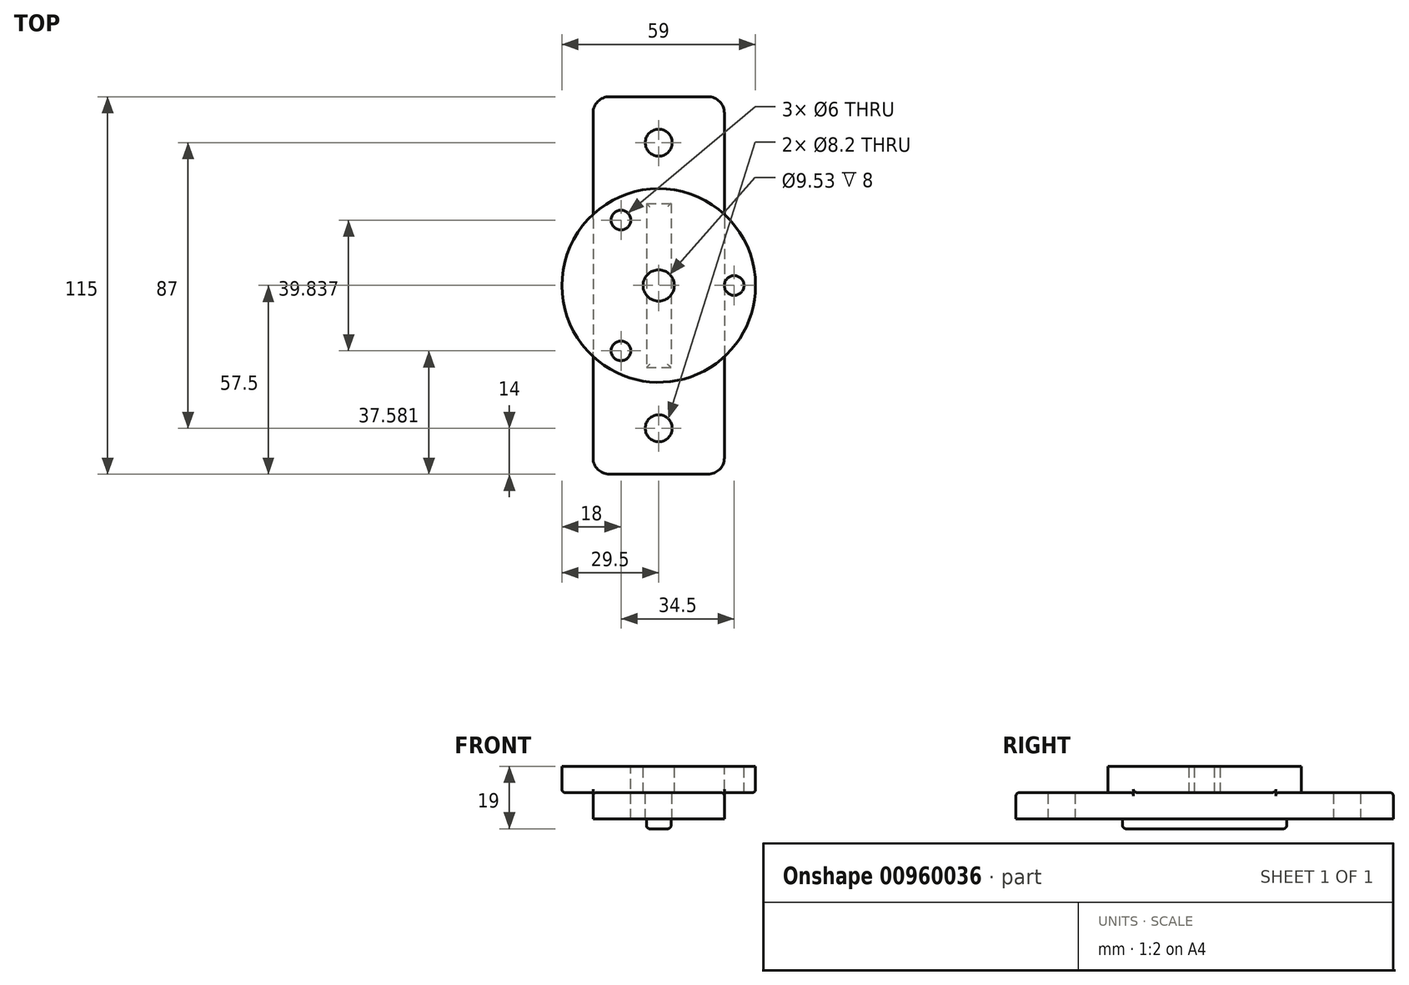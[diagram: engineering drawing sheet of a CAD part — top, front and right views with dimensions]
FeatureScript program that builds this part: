
annotation { "Feature Type Name" : "Feature", "Feature Type Description" : "" }
export const myFeature = defineFeature(function(context is Context, id is Id, definition is map)
    precondition{}
    {
        {
            var Q0;
            Q0=qCreatedBy(makeId("Top.planeOp"),FACE);
            var sketch = newSketch(context, id + "F0", { "sketchPlane" : qUnion([Q0])});
            skLineSegment(sketch, "E0.bottom", {"start": v(20, 57.5) * mm, "end": v(-20, 57.5) * mm});
            skLineSegment(sketch, "E0.top", {"start": v(20, -57.5) * mm, "end": v(-20, -57.5) * mm});
            skLineSegment(sketch, "E0.left", {"start": v(20, 57.5) * mm, "end": v(20, -57.5) * mm});
            skLineSegment(sketch, "E0.right", {"start": v(-20, 57.5) * mm, "end": v(-20, -57.5) * mm});
            skPoint(sketch, "E0.middle", {"position": v(0, 0) * mm});
            skCircle(sketch, "E1", {"center": v(0, 0) * mm, "radius": 29.5 * mm});
            skPoint(sketch, "E2", {"position": v(0, -43.5) * mm});
            skCircle(sketch, "E3", {"center": v(0, -43.5) * mm, "radius": 4.1 * mm});
            skPoint(sketch, "E4", {"position": v(0, 43.5) * mm});
            skCircle(sketch, "E5", {"center": v(0, 43.5) * mm, "radius": 4.1 * mm});
            skSolve(sketch);
        }
        {
            var Q0;
            {var subQ5=sQuery(id+"F0.wireOp",EDGE,"E0.bottom");Q0=makeQuery(id+"F0.imprint","IMPRINT",FACE,{"disambiguationData":[TD([[makeQuery(id+"F0.imprint","IMPRINT",EDGE,{"derivedFrom":subQ5}),1.0]])]});}
            var Q1;
            {var subQ5=sQuery(id+"F0.wireOp",EDGE,"E0.top");Q1=makeQuery(id+"F0.imprint","IMPRINT",FACE,{"disambiguationData":[TD([[makeQuery(id+"F0.imprint","IMPRINT",EDGE,{"derivedFrom":subQ5}),-1.0]])]});}
            var Q2;
            {var subQ0=sQuery(id+"F0.wireOp",EDGE,"E1");var subQ1=sQuery(id+"F0.wireOp",EDGE,"E0.left");var subQ2=makeQuery(id+"F0.imprint","INTERSECT",VERTEX,{"disambiguationData":[OD(0.0)],"derivedFrom":[subQ1,subQ0]});Q2=makeQuery(id+"F0.imprint","IMPRINT",FACE,{"disambiguationData":[TD([[makeQuery(id+"F0.imprint","IMPRINT",EDGE,{"disambiguationData":[TD([[subQ2,-1.0]])],"derivedFrom":subQ1}),-1.0]])]});}
            extrude(context, id + "F1", {"entities" : qUnion([Q0, Q1, Q2]), "oppositeDirection" : true, "depth" : 8 * mm, "offsetDistance" : 25 * mm});
        }
        {
            var Q0;
            {var subQ0=sQuery(id+"F0.wireOp",EDGE,"E1");var subQ1=sQuery(id+"F0.wireOp",EDGE,"E0.left");var subQ2=makeQuery(id+"F0.imprint","INTERSECT",VERTEX,{"disambiguationData":[OD(0.0)],"derivedFrom":[subQ1,subQ0]});Q0=makeQuery(id+"F0.imprint","IMPRINT",FACE,{"disambiguationData":[TD([[makeQuery(id+"F0.imprint","IMPRINT",EDGE,{"disambiguationData":[TD([[subQ2,-1.0]])],"derivedFrom":subQ1}),1.0]])]});}
            var Q1;
            {var subQ0=sQuery(id+"F0.wireOp",EDGE,"E1");var subQ1=sQuery(id+"F0.wireOp",EDGE,"E0.right");var subQ2=makeQuery(id+"F0.imprint","INTERSECT",VERTEX,{"disambiguationData":[OD(0.0)],"derivedFrom":[subQ1,subQ0]});Q1=makeQuery(id+"F0.imprint","IMPRINT",FACE,{"disambiguationData":[TD([[makeQuery(id+"F0.imprint","IMPRINT",EDGE,{"disambiguationData":[TD([[subQ2,-1.0]])],"derivedFrom":subQ1}),-1.0]])]});}
            var Q2;
            {var subQ0=sQuery(id+"F0.wireOp",EDGE,"E1");var subQ1=sQuery(id+"F0.wireOp",EDGE,"E0.left");var subQ2=makeQuery(id+"F0.imprint","INTERSECT",VERTEX,{"disambiguationData":[OD(0.0)],"derivedFrom":[subQ1,subQ0]});Q2=makeQuery(id+"F0.imprint","IMPRINT",FACE,{"disambiguationData":[TD([[makeQuery(id+"F0.imprint","IMPRINT",EDGE,{"disambiguationData":[TD([[subQ2,-1.0]])],"derivedFrom":subQ1}),-1.0]])]});}
            extrude(context, id + "F2", {"entities" : qUnion([Q0, Q1, Q2]), "operationType" : NewBodyOperationType.ADD, "depth" : 8 * mm, "offsetDistance" : 25 * mm});
        }
        {
            var Q0;
            Q0=makeQuery(id+"F1.opExtrude","SWEPT_EDGE",EDGE,{"disambiguationData":[OSD([sQuery(id+"F0.wireOp",EDGE,"E0.top"),sQuery(id+"F0.wireOp",EDGE,"E0.right")])]});
            var Q1;
            Q1=makeQuery(id+"F1.opExtrude","SWEPT_EDGE",EDGE,{"disambiguationData":[OSD([sQuery(id+"F0.wireOp",EDGE,"E0.top"),sQuery(id+"F0.wireOp",EDGE,"E0.left")])]});
            var Q2;
            Q2=makeQuery(id+"F1.opExtrude","SWEPT_EDGE",EDGE,{"disambiguationData":[OSD([sQuery(id+"F0.wireOp",EDGE,"E0.bottom"),sQuery(id+"F0.wireOp",EDGE,"E0.right")])]});
            var Q3;
            Q3=makeQuery(id+"F1.opExtrude","SWEPT_EDGE",EDGE,{"disambiguationData":[OSD([sQuery(id+"F0.wireOp",EDGE,"E0.bottom"),sQuery(id+"F0.wireOp",EDGE,"E0.left")])]});
            fillet(context, id + "F3", {"entities" : qUnion([Q0, Q1, Q2, Q3]), "radius" : 5 * mm, "tangentPropagation" : true, "allowEdgeOverflow" : false});
        }
        {
            var Q0;
            {var subQ0=sQuery(id+"F0.wireOp",EDGE,"E0.left");var subQ1=makeQuery(id+"F1.opExtrude","SWEPT_FACE",FACE,{"disambiguationData":[OSD([subQ0])]});var subQ3=sQuery(id+"F0.wireOp",EDGE,"E0.top");var subQ4=makeQuery(id+"F1.opExtrude","CAP_FACE",FACE,{"disambiguationData":[OSD([sQuery(id+"F0.wireOp",EDGE,"E0.bottom"),subQ3,subQ0,sQuery(id+"F0.wireOp",EDGE,"E0.right"),sQuery(id+"F0.wireOp",EDGE,"E3"),sQuery(id+"F0.wireOp",EDGE,"E5")])],"isStart":true});Q0=makeQuery(id+"F2.boolean.opBoolean","SPLIT",EDGE,{"disambiguationData":[topologyDisambiguationEdgeConnected([subQ4,subQ1]),TD([makeQuery(id+"F1.opExtrude","SWEPT_FACE",FACE,{"disambiguationData":[OSD([subQ3])]})])],"derivedFrom":makeQuery(id+"F1.opExtrude","CAP_EDGE",EDGE,{"disambiguationData":[OSD([subQ0])],"isStart":true})});}
            var Q1;
            {var subQ0=sQuery(id+"F0.wireOp",EDGE,"E0.left");var subQ1=makeQuery(id+"F1.opExtrude","SWEPT_FACE",FACE,{"disambiguationData":[OSD([subQ0])]});var subQ3=sQuery(id+"F0.wireOp",EDGE,"E0.bottom");var subQ4=makeQuery(id+"F1.opExtrude","CAP_FACE",FACE,{"disambiguationData":[OSD([subQ3,sQuery(id+"F0.wireOp",EDGE,"E0.top"),subQ0,sQuery(id+"F0.wireOp",EDGE,"E0.right"),sQuery(id+"F0.wireOp",EDGE,"E3"),sQuery(id+"F0.wireOp",EDGE,"E5")])],"isStart":true});Q1=makeQuery(id+"F2.boolean.opBoolean","SPLIT",EDGE,{"disambiguationData":[topologyDisambiguationEdgeConnected([subQ4,subQ1]),TD([makeQuery(id+"F1.opExtrude","SWEPT_FACE",FACE,{"disambiguationData":[OSD([subQ3])]})])],"derivedFrom":makeQuery(id+"F1.opExtrude","CAP_EDGE",EDGE,{"disambiguationData":[OSD([subQ0])],"isStart":true})});}
            fillet(context, id + "F4", {"entities" : qUnion([Q0, Q1]), "radius" : 1 * mm, "tangentPropagation" : true, "allowEdgeOverflow" : false});
        }
        {
            var Q0;
            {var subQ0=sQuery(id+"F0.wireOp",EDGE,"E0.left");var subQ1=sQuery(id+"F0.wireOp",EDGE,"E1");var subQ2=makeQuery(id+"F2.opExtrude","SWEPT_FACE",FACE,{"disambiguationData":[OSD([subQ1])]});var subQ3=makeQuery(id+"F2.opExtrude","CAP_FACE",FACE,{"disambiguationData":[OSD([subQ1])],"isStart":true});Q0=makeQuery(id+"F2.boolean.opBoolean","SPLIT",EDGE,{"disambiguationData":[topologyDisambiguationEdgeConnected([subQ2,subQ3]),TD([makeQuery(id+"F1.opExtrude","SWEPT_FACE",FACE,{"disambiguationData":[OSD([subQ0])]})])],"derivedFrom":makeQuery(id+"F2.opExtrude","CAP_EDGE",EDGE,{"disambiguationData":[OSD([subQ1])],"isStart":true})});}
            var Q1;
            {var subQ0=sQuery(id+"F0.wireOp",EDGE,"E0.right");var subQ1=sQuery(id+"F0.wireOp",EDGE,"E1");var subQ2=makeQuery(id+"F2.opExtrude","SWEPT_FACE",FACE,{"disambiguationData":[OSD([subQ1])]});var subQ3=makeQuery(id+"F2.opExtrude","CAP_FACE",FACE,{"disambiguationData":[OSD([subQ1])],"isStart":true});Q1=makeQuery(id+"F2.boolean.opBoolean","SPLIT",EDGE,{"disambiguationData":[topologyDisambiguationEdgeConnected([subQ2,subQ3]),TD([makeQuery(id+"F1.opExtrude","SWEPT_FACE",FACE,{"disambiguationData":[OSD([subQ0])]})])],"derivedFrom":makeQuery(id+"F2.opExtrude","CAP_EDGE",EDGE,{"disambiguationData":[OSD([subQ1])],"isStart":true})});}
            fillet(context, id + "F5", {"entities" : qUnion([Q0, Q1]), "radius" : 1 * mm, "tangentPropagation" : true, "allowEdgeOverflow" : false});
        }
        {
            var Q0;
            Q0=makeQuery(id+"F2.opExtrude","CAP_FACE",FACE,{"disambiguationData":[OSD([sQuery(id+"F0.wireOp",EDGE,"E1")])],"isStart":false});
            var sketch = newSketch(context, id + "F6", { "sketchPlane" : qUnion([Q0])});
            skPoint(sketch, "E6", {"position": v(23, 0) * mm});
            skPoint(sketch, "E7", {"position": v(-11.5, -19.92) * mm});
            skPoint(sketch, "E8", {"position": v(-11.5, 19.92) * mm});
            skPoint(sketch, "E9", {"position": v(0, 0) * mm});
            skCircle(sketch, "E10", {"center": v(0, 0) * mm, "radius": 4.76 * mm});
            skCircle(sketch, "E11", {"center": v(23, 0) * mm, "radius": 3 * mm});
            skCircle(sketch, "E12", {"center": v(-11.5, 19.92) * mm, "radius": 3 * mm});
            skCircle(sketch, "E13", {"center": v(-11.5, -19.92) * mm, "radius": 3 * mm});
            skSolve(sketch);
        }
        {
            var Q0;
            Q0=makeQuery(id+"F1.opExtrude","CAP_FACE",FACE,{"disambiguationData":[OSD([sQuery(id+"F0.wireOp",EDGE,"E0.bottom"),sQuery(id+"F0.wireOp",EDGE,"E0.top"),sQuery(id+"F0.wireOp",EDGE,"E0.left"),sQuery(id+"F0.wireOp",EDGE,"E0.right"),sQuery(id+"F0.wireOp",EDGE,"E3"),sQuery(id+"F0.wireOp",EDGE,"E5")])],"isStart":false});
            var sketch = newSketch(context, id + "F7", { "sketchPlane" : qUnion([Q0])});
            skLineSegment(sketch, "E14.bottom", {"start": v(-3.75, -25) * mm, "end": v(3.75, -25) * mm});
            skLineSegment(sketch, "E14.top", {"start": v(-3.75, 25) * mm, "end": v(3.75, 25) * mm});
            skLineSegment(sketch, "E14.left", {"start": v(-3.75, -25) * mm, "end": v(-3.75, 25) * mm});
            skLineSegment(sketch, "E14.right", {"start": v(3.75, -25) * mm, "end": v(3.75, 25) * mm});
            skPoint(sketch, "E14.middle", {"position": v(0, 0) * mm});
            skSolve(sketch);
        }
        {
            var Q0;
            Q0=qSketchRegion(id+"F7",true);
            extrude(context, id + "F8", {"entities" : qUnion([Q0]), "operationType" : NewBodyOperationType.ADD, "depth" : 3 * mm, "offsetDistance" : 25 * mm});
        }
        {
            var Q0;
            Q0=makeQuery(id+"F8.opExtrude","CAP_EDGE",EDGE,{"disambiguationData":[OSD([sQuery(id+"F7.wireOp",EDGE,"E14.bottom")])],"isStart":false});
            var Q1;
            Q1=makeQuery(id+"F8.opExtrude","CAP_EDGE",EDGE,{"disambiguationData":[OSD([sQuery(id+"F7.wireOp",EDGE,"E14.right")])],"isStart":false});
            var Q2;
            Q2=makeQuery(id+"F8.opExtrude","CAP_EDGE",EDGE,{"disambiguationData":[OSD([sQuery(id+"F7.wireOp",EDGE,"E14.left")])],"isStart":false});
            var Q3;
            Q3=makeQuery(id+"F8.opExtrude","CAP_EDGE",EDGE,{"disambiguationData":[OSD([sQuery(id+"F7.wireOp",EDGE,"E14.top")])],"isStart":false});
            fillet(context, id + "F9", {"entities" : qUnion([Q0, Q1, Q2, Q3]), "radius" : 1 * mm, "tangentPropagation" : true, "allowEdgeOverflow" : false});
        }
        {
            var Q0;
            Q0=makeQuery(id+"F6.imprint","IMPRINT",FACE,{"disambiguationData":[TD([[makeQuery(id+"F6.imprint","IMPRINT",EDGE,{"derivedFrom":sQuery(id+"F6.wireOp",EDGE,"E13")}),1.0]])]});
            var Q1;
            Q1=makeQuery(id+"F6.imprint","IMPRINT",FACE,{"disambiguationData":[TD([[makeQuery(id+"F6.imprint","IMPRINT",EDGE,{"derivedFrom":sQuery(id+"F6.wireOp",EDGE,"E11")}),1.0]])]});
            var Q2;
            Q2=makeQuery(id+"F6.imprint","IMPRINT",FACE,{"disambiguationData":[TD([[makeQuery(id+"F6.imprint","IMPRINT",EDGE,{"derivedFrom":sQuery(id+"F6.wireOp",EDGE,"E12")}),1.0]])]});
            extrude(context, id + "F10", {"entities" : qUnion([Q0, Q1, Q2]), "operationType" : NewBodyOperationType.REMOVE, "oppositeDirection" : true, "depth" : 17 * mm, "offsetDistance" : 25 * mm});
        }
        {
            var Q0;
            Q0=makeQuery(id+"F6.imprint","IMPRINT",FACE,{"disambiguationData":[TD([[makeQuery(id+"F6.imprint","IMPRINT",EDGE,{"derivedFrom":sQuery(id+"F6.wireOp",EDGE,"E10")}),1.0]])]});
            extrude(context, id + "F11", {"entities" : qUnion([Q0]), "operationType" : NewBodyOperationType.REMOVE, "oppositeDirection" : true, "depth" : 8 * mm, "offsetDistance" : 25 * mm});
        }
    });
